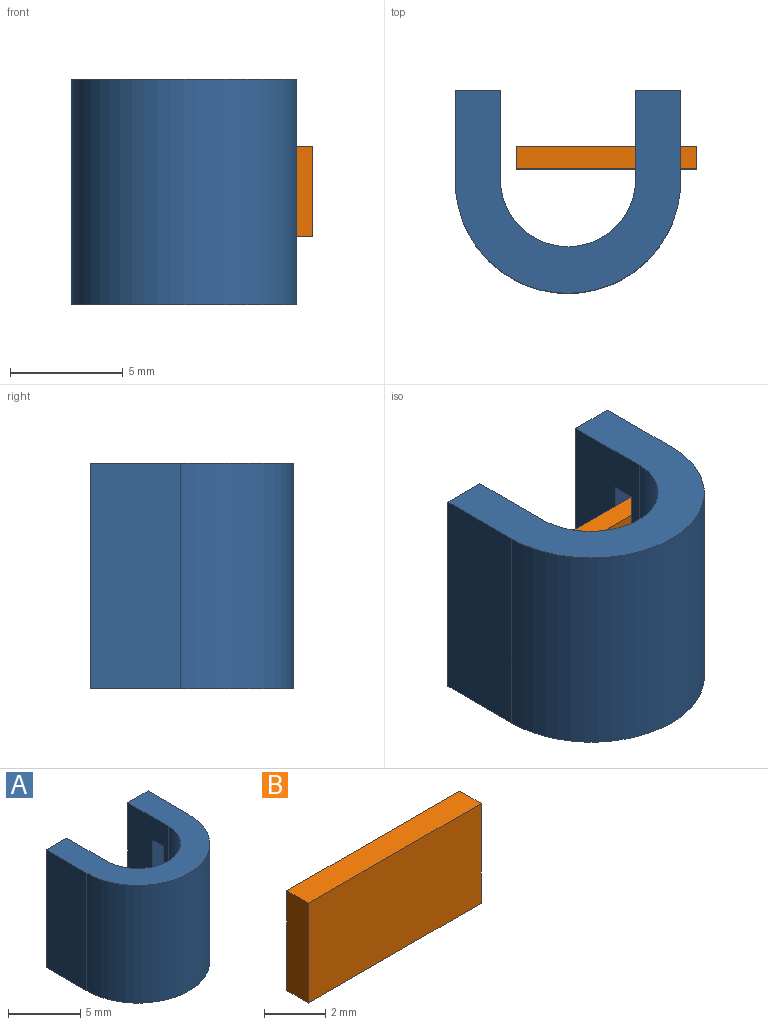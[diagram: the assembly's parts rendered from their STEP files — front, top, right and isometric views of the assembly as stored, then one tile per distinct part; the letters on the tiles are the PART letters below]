
ASSEMBLY  parts=2 mates=1
PART A: 19 faces, bbox 10x9x10 mm
  f0: plane 10x4mm, normal (1,0,0), area 34mm2, adj f3,f4,f8,f9,f10,f11,f12,f13
  f1: plane 10x4mm, normal (-1,0,0), area 34mm2, adj f4,f5,f8,f9,f10,f11,f12,f13
  f2: plane 10x4mm, normal (-1,0,0), area 40mm2, adj f3,f7,f8,f9
  f3: cylinder r=5mm len=10mm, axis (0,0,-1), area 157.1mm2, adj f0,f2,f8,f9
  f4: plane 10x2mm, normal (0,1,0), area 20mm2, adj f0,f1,f8,f9
  f5: cylinder r=3mm len=10mm, axis (0,0,-1), area 92.9mm2, adj f1,f6,f8,f9
  f6: plane 10x4mm, normal (1,0,0), area 34mm2, adj f5,f7,f8,f9,f14,f15,f16,f17
  f7: plane 10x2mm, normal (0,1,0), area 20mm2, adj f2,f6,f8,f9
  f8: plane 10x9mm, normal (0,0,1), area 41.5mm2, adj f0,f1,f2,f3,f4,f5,f6,f7
  f9: plane 10x9mm, normal (0,0,-1), area 41.5mm2, adj f0,f1,f2,f3,f4,f5,f6,f7
  f10: plane 2x1mm, normal (0,0,-1), area 2mm2, adj f0,f1,f11,f13
  f11: plane 6x2mm, normal (0,-1,0), area 12mm2, adj f0,f1,f10,f12
  f12: plane 2x1mm, normal (0,0,1), area 2mm2, adj f0,f1,f11,f13
  f13: plane 6x2mm, normal (0,1,0), area 12mm2, adj f0,f1,f10,f12
  f14: plane 1x0.5mm, normal (0,0,-1), area 0.5mm2, adj f6,f15,f17,f18
  f15: plane 6x0.5mm, normal (0,-1,0), area 3mm2, adj f6,f14,f16,f18
  f16: plane 1x0.5mm, normal (0,0,1), area 0.5mm2, adj f6,f15,f17,f18
  f17: plane 6x0.5mm, normal (0,1,0), area 3mm2, adj f6,f14,f16,f18
  f18: plane 6x1mm, normal (1,0,0), area 6mm2, adj f14,f15,f16,f17
PART B: 6 faces, bbox 8x1x4 mm
  f0: plane 8x4mm, normal (0,1,0), area 32mm2, adj f1,f3,f4,f5
  f1: plane 4x1mm, normal (-1,0,0), area 4mm2, adj f0,f2,f4,f5
  f2: plane 8x4mm, normal (0,-1,0), area 32mm2, adj f1,f3,f4,f5
  f3: plane 4x1mm, normal (1,0,0), area 4mm2, adj f0,f2,f4,f5
  f4: plane 8x1mm, normal (0,0,1), area 8mm2, adj f0,f1,f2,f3
  f5: plane 8x1mm, normal (0,0,-1), area 8mm2, adj f0,f1,f2,f3
PLACE A t=(6.21,-1.51,0.83)mm
PLACE B rot(axis=(0,1,0),180deg) t=(-15.68,0.01,7.86)mm
MATE slider B.f3 <-> A.f18  axis (-1,0,0) through (-1.08,-0.49,5.86)mm
